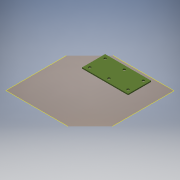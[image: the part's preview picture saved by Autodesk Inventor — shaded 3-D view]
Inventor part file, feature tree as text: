
AUTODESK INVENTOR PART (.ipt)
format: ipt  version: 2016 (Build 200138000, 138)  size: 110,080 bytes
history: native  units: mm
features: reference x6, plane x1, extrude x1, sketch x1
ambient origin geometry x8: Origin, YZ Plane, XZ Plane, XY Plane, X Axis, Y Axis, Z Axis, Center Point
bodies: Solid1 (feature_tree)
feature tree (9):
  plane  "Work Plane1"
  extrude  "Extrusion1"  Depth=1.75mm
  sketch  "Sketch2"  dims[d0=6.0mm d1=6.0mm d2=6.0mm d3=6.0mm d4=0.4mm d5=0.4mm d6=0.4mm d7=0.4mm d8=0.4mm d9=0.4mm d10=1.75mm d11=0.0mm]
  reference  "Reference1"
  reference  "Reference2"
  reference  "Reference3"
  reference  "Reference4"
  reference  "Reference5"
  reference  "Reference6"
